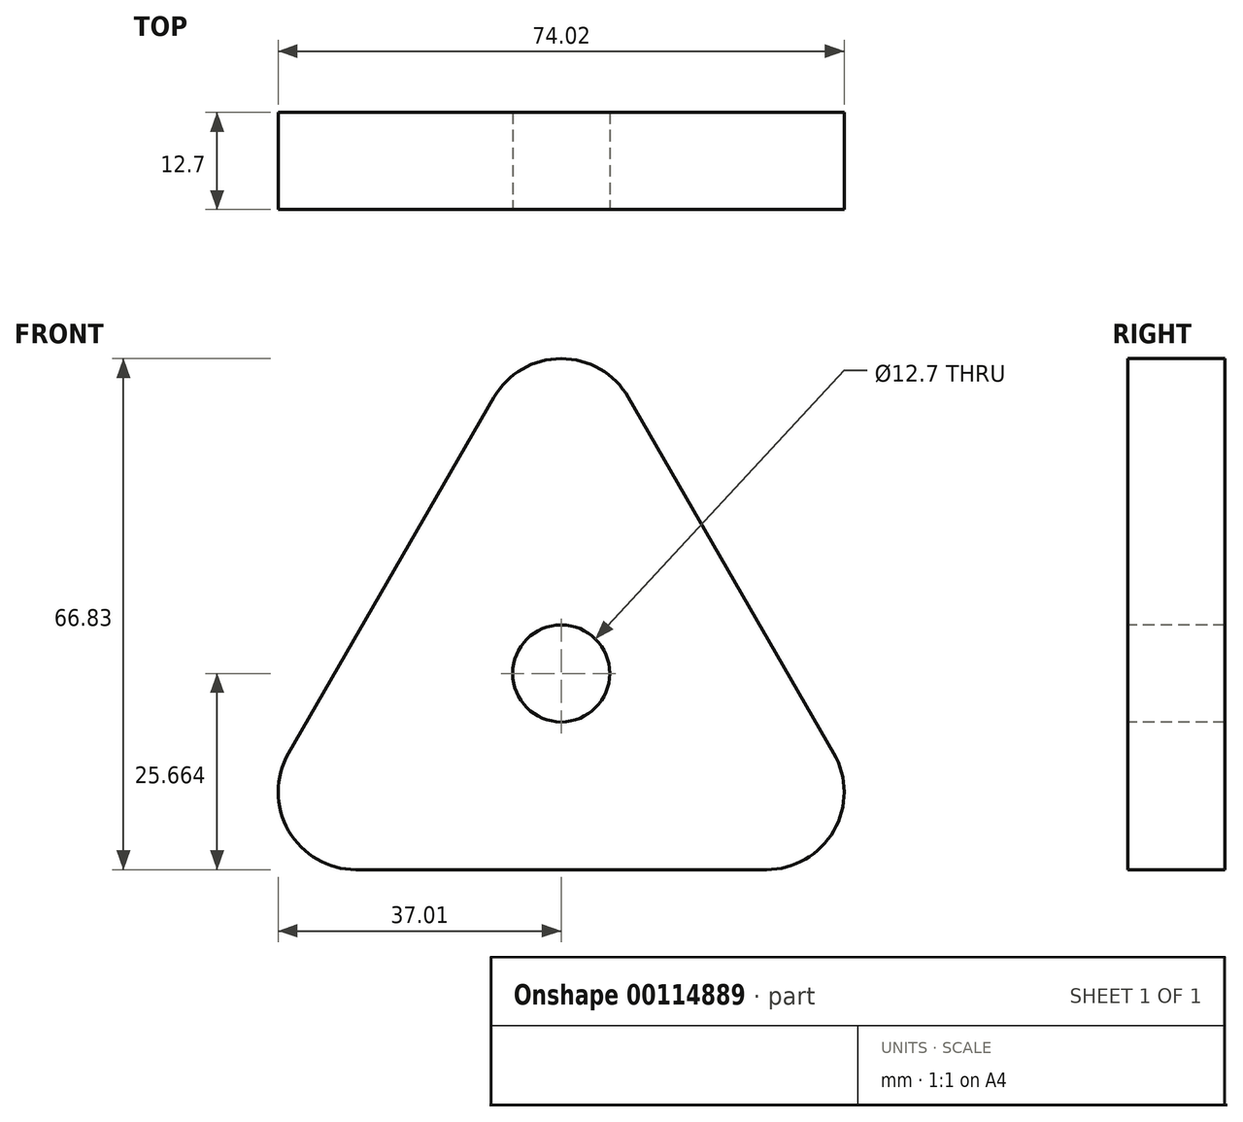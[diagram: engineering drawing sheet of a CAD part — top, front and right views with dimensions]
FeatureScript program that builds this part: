
annotation { "Feature Type Name" : "Feature", "Feature Type Description" : "" }
export const myFeature = defineFeature(function(context is Context, id is Id, definition is map)
    precondition{}
    {
        {
            var Q0;
            Q0=qCreatedBy(makeId("Front.planeOp"),FACE);
            var sketch = newSketch(context, id + "F0", { "sketchPlane" : qUnion([Q0])});
            skLineSegment(sketch, "E0", {"start": v(0, 0) * mm, "end": v(0, 25.4) * mm, "construction": true});
            skLineSegment(sketch, "E1", {"start": v(0, 0) * mm, "end": v(0, -25.4) * mm, "construction": true});
            skLineSegment(sketch, "E2", {"start": v(-8.8, 10.16) * mm, "end": v(-35.65, -36.35) * mm});
            skLineSegment(sketch, "E3", {"start": v(8.8, 10.16) * mm, "end": v(35.65, -36.35) * mm});
            skLineSegment(sketch, "E4", {"start": v(-26.85, -51.59) * mm, "end": v(26.85, -51.59) * mm});
            skLineSegment(sketch, "E5", {"start": v(-33.48, 0) * mm, "end": v(43.4, 0) * mm, "construction": true});
            skPoint(sketch, "E6.visualSharp", {"position": v(0, 25.4) * mm});
            skArc(sketch, "E6.filletArc", {"start": v(8.8, 10.16) * mm, "mid": v(0, 15.24) * mm, "end": v(-8.8, 10.16) * mm});
            skPoint(sketch, "E7.visualSharp", {"position": v(-44.45, -51.59) * mm});
            skArc(sketch, "E7.filletArc", {"start": v(-35.65, -36.35) * mm, "mid": v(-35.65, -46.5) * mm, "end": v(-26.85, -51.59) * mm});
            skPoint(sketch, "E8.visualSharp", {"position": v(44.45, -51.59) * mm});
            skArc(sketch, "E8.filletArc", {"start": v(26.85, -51.59) * mm, "mid": v(35.65, -46.5) * mm, "end": v(35.65, -36.35) * mm});
            skLineSegment(sketch, "E9", {"start": v(0, 0) * mm, "end": v(14.66, 0) * mm, "construction": true});
            skLineSegment(sketch, "E10", {"start": v(0, 0) * mm, "end": v(-14.66, 0) * mm, "construction": true});
            skSolve(sketch);
        }
        {
            var Q0;
            Q0 = qSketchRegion(id + "F0", true);
            extrude(context, id + "F1", {"entities" : qUnion([Q0]), "depth" : 12.7 * mm});
        }
        {
            var Q0;
            Q0=makeQuery(id+"F1.opExtrude","CAP_FACE",FACE,{"disambiguationData":[OSD([sQuery(id+"F0.wireOp",EDGE,"E2"),sQuery(id+"F0.wireOp",EDGE,"E3"),sQuery(id+"F0.wireOp",EDGE,"E4"),sQuery(id+"F0.wireOp",EDGE,"E6.filletArc"),sQuery(id+"F0.wireOp",EDGE,"E7.filletArc"),sQuery(id+"F0.wireOp",EDGE,"E8.filletArc")])],"isStart":false});
            var sketch = newSketch(context, id + "F2", { "sketchPlane" : qUnion([Q0])});
            skLineSegment(sketch, "E11", {"start": v(-35.65, -46.5) * mm, "end": v(0, -25.93) * mm, "construction": true});
            skLineSegment(sketch, "E12", {"start": v(0, 15.24) * mm, "end": v(0, -25.93) * mm, "construction": true});
            skLineSegment(sketch, "E13", {"start": v(35.65, -46.5) * mm, "end": v(0, -25.93) * mm, "construction": true});
            skCircle(sketch, "E14", {"center": v(0, -25.93) * mm, "radius": 6.35 * mm});
            skSolve(sketch);
        }
        {
            var Q0;
            Q0=makeQuery(id+"F2.imprint","IMPRINT",FACE,{"disambiguationData":[TD([[makeQuery(id+"F2.imprint","IMPRINT",EDGE,{"derivedFrom":sQuery(id+"F2.wireOp",EDGE,"E14")}),1.0]])]});
            var Q1;
            Q1=sQuery(id+"F2.wireOp",EDGE,"QFnR3G9j-Mm4j-uMxI-Hg1k-K7k4eNcVNfiD");
            extrude(context, id + "F3", {"entities" : qUnion([Q0]), "operationType" : NewBodyOperationType.REMOVE, "surfaceEntities" : qUnion([Q1]), "oppositeDirection" : true, "depth" : 25.4 * mm});
        }
    });
